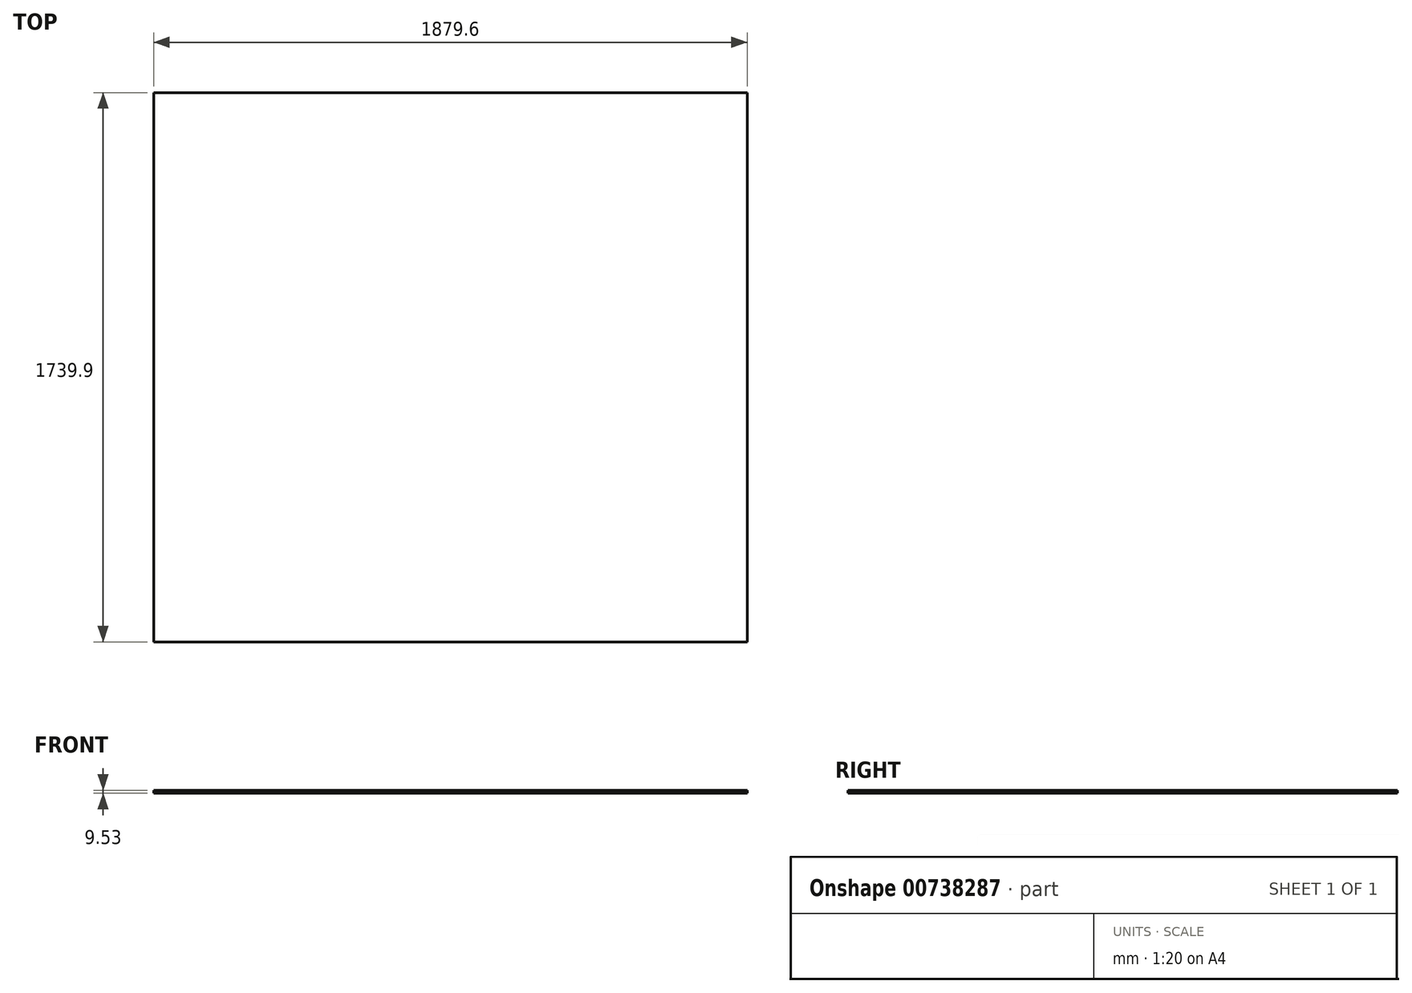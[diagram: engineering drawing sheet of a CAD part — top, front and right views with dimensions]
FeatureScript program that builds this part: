
annotation { "Feature Type Name" : "Feature", "Feature Type Description" : "" }
export const myFeature = defineFeature(function(context is Context, id is Id, definition is map)
    precondition{}
    {
        {
            var Q0;
            Q0=qCreatedBy(makeId("Top.planeOp"),FACE);
            var sketch = newSketch(context, id + "F0", { "sketchPlane" : qUnion([Q0])});
            skLineSegment(sketch, "E0.bottom", {"start": v(939.8, 869.95) * mm, "end": v(-939.8, 869.95) * mm});
            skLineSegment(sketch, "E0.top", {"start": v(939.8, -869.95) * mm, "end": v(-939.8, -869.95) * mm});
            skLineSegment(sketch, "E0.left", {"start": v(939.8, 869.95) * mm, "end": v(939.8, -869.95) * mm});
            skLineSegment(sketch, "E0.right", {"start": v(-939.8, 869.95) * mm, "end": v(-939.8, -869.95) * mm});
            skPoint(sketch, "E0.middle", {"position": v(0, 0) * mm});
            skSolve(sketch);
        }
        {
            var Q0;
            Q0=makeQuery(id+"F0.imprint","IMPRINT",FACE,{"disambiguationData":[TD([[makeQuery(id+"F0.imprint","IMPRINT",EDGE,{"derivedFrom":sQuery(id+"F0.wireOp",EDGE,"E0.bottom")}),1.0]])]});
            extrude(context, id + "F1", {"entities" : qUnion([Q0]), "depth" : 9.52 * mm, "offsetDistance" : 25.4 * mm});
        }
    });
